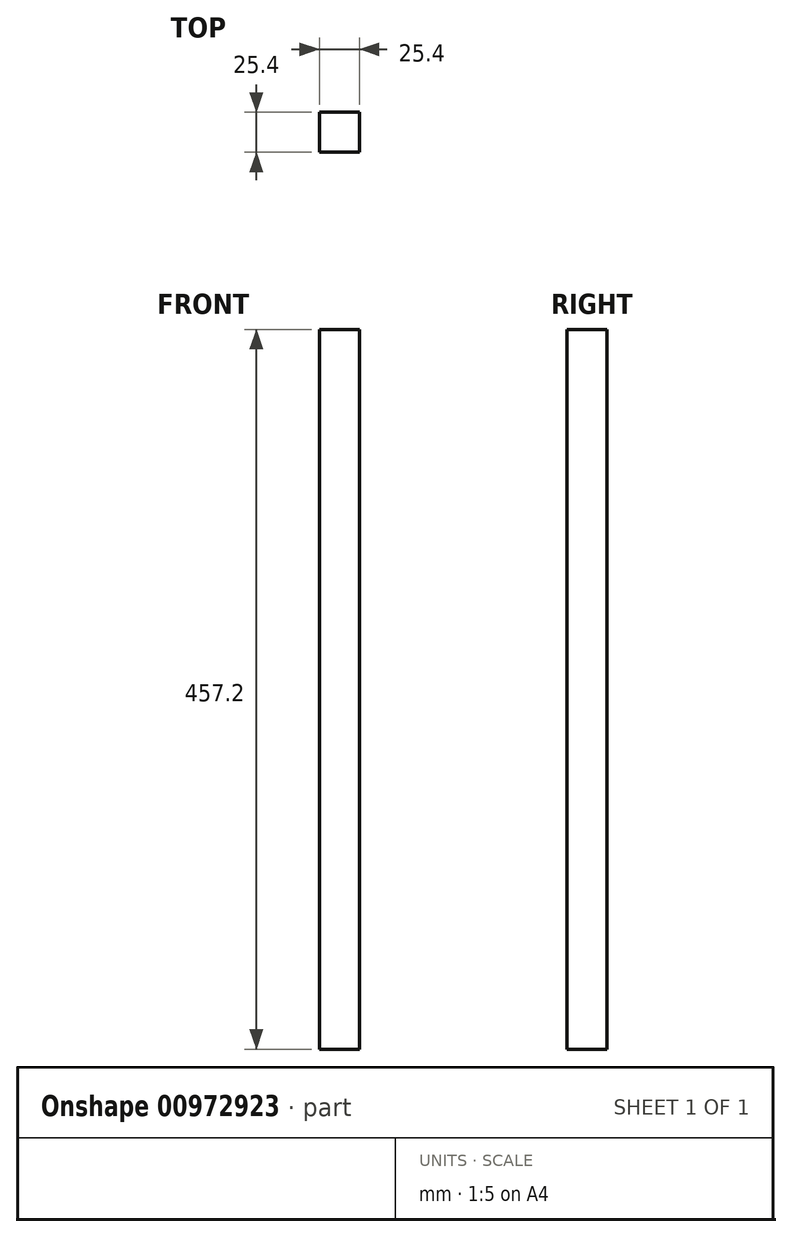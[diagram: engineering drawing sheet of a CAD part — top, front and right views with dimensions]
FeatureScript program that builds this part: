
annotation { "Feature Type Name" : "Feature", "Feature Type Description" : "" }
export const myFeature = defineFeature(function(context is Context, id is Id, definition is map)
    precondition{}
    {
        {
            var Q0;
            Q0=qCreatedBy(makeId("Top.planeOp"),FACE);
            var sketch = newSketch(context, id + "F0", { "sketchPlane" : qUnion([Q0])});
            skLineSegment(sketch, "E0.bottom", {"start": v(-38.23, 21.16) * mm, "end": v(-12.83, 21.16) * mm});
            skLineSegment(sketch, "E0.top", {"start": v(-38.23, -4.24) * mm, "end": v(-12.83, -4.24) * mm});
            skLineSegment(sketch, "E0.left", {"start": v(-38.23, 21.16) * mm, "end": v(-38.23, -4.24) * mm});
            skLineSegment(sketch, "E0.right", {"start": v(-12.83, 21.16) * mm, "end": v(-12.83, -4.24) * mm});
            skSolve(sketch);
        }
        {
            var Q0;
            Q0=makeQuery(id+"F0.imprint","IMPRINT",FACE,{"disambiguationData":[TD([[makeQuery(id+"F0.imprint","IMPRINT",EDGE,{"derivedFrom":sQuery(id+"F0.wireOp",EDGE,"E0.bottom")}),-1.0]])]});
            extrude(context, id + "F1", {"entities" : qUnion([Q0]), "depth" : 457.2 * mm, "offsetDistance" : 25.4 * mm});
        }
    });
